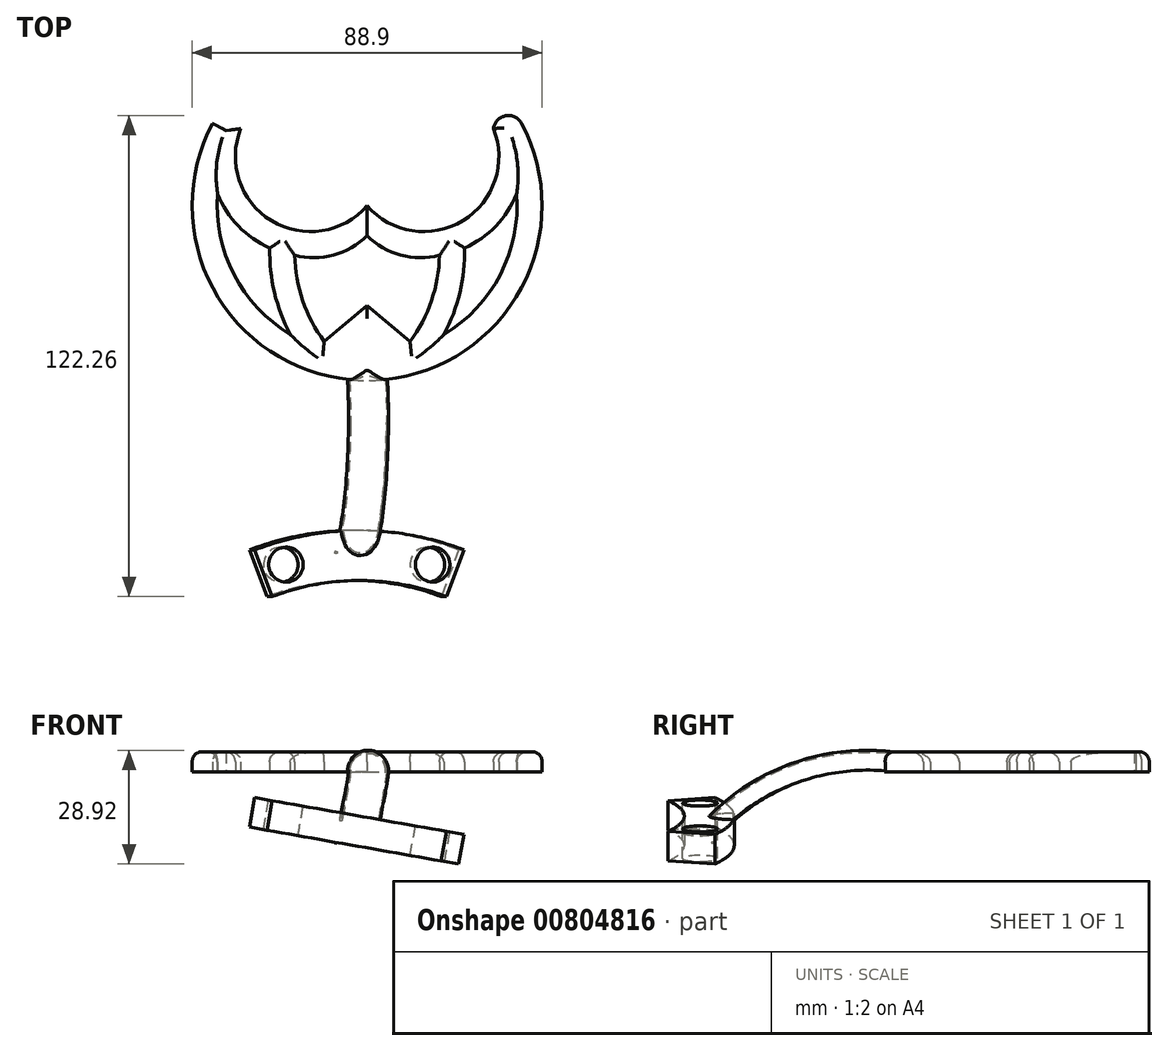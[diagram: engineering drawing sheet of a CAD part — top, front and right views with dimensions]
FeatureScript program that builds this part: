
annotation { "Feature Type Name" : "Feature", "Feature Type Description" : "" }
export const myFeature = defineFeature(function(context is Context, id is Id, definition is map)
    precondition{}
    {
        {
            var Q0;
            Q0=qCreatedBy(makeId("Top.planeOp"),FACE);
            var sketch = newSketch(context, id + "F0", { "sketchPlane" : qUnion([Q0])});
            skArc(sketch, "E0", {"start": v(-39.25, 20.86) * mm, "mid": v(0, -44.45) * mm, "end": v(39.25, 20.86) * mm});
            skPoint(sketch, "E1", {"position": v(0, -44.45) * mm});
            skArc(sketch, "E2", {"start": v(-39.25, 20.86) * mm, "mid": v(-35.2, 22.82) * mm, "end": v(-32.1, 19.54) * mm});
            skLineSegment(sketch, "E3", {"start": v(-35.88, 19.08) * mm, "end": v(-39.25, 20.86) * mm});
            skLineSegment(sketch, "E4", {"start": v(-35.88, 19.08) * mm, "end": v(-32.1, 19.54) * mm});
            skArc(sketch, "E5", {"start": v(-32.1, 19.54) * mm, "mid": v(-24.33, -3.83) * mm, "end": v(0, 0) * mm});
            skPoint(sketch, "E6", {"position": v(0, -25.4) * mm});
            skLineSegment(sketch, "E7", {"start": v(0, -44.45) * mm, "end": v(0, -25.4) * mm});
            skLineSegment(sketch, "E8", {"start": v(0, -25.4) * mm, "end": v(-18.1, -40.6) * mm});
            skArc(sketch, "E9", {"start": v(-17.99, -6.27) * mm, "mid": v(-14.76, -28.08) * mm, "end": v(0, -44.45) * mm});
            skLineSegment(sketch, "E10", {"start": v(0, 0) * mm, "end": v(0, -7.62) * mm});
            skArc(sketch, "E11", {"start": v(-18.39, -12.6) * mm, "mid": v(-8.53, -12.58) * mm, "end": v(0, -7.62) * mm});
            skArc(sketch, "E12", {"start": v(-24.73, -10.77) * mm, "mid": v(-23.55, -22.07) * mm, "end": v(-19.55, -32.7) * mm});
            skArc(sketch, "E13", {"start": v(-37.99, 2.95) * mm, "mid": v(-32.7, -5.2) * mm, "end": v(-24.73, -10.77) * mm});
            skArc(sketch, "E14", {"start": v(-37.99, 2.95) * mm, "mid": v(-33.84, -17.5) * mm, "end": v(-19.55, -32.7) * mm});
            skArc(sketch, "E15.MirrorCS", {"start": v(32.1, 19.54) * mm, "mid": v(24.33, -3.83) * mm, "end": v(0, 0) * mm});
            skArc(sketch, "E16.MirrorCS", {"start": v(39.25, 20.86) * mm, "mid": v(35.2, 22.82) * mm, "end": v(32.1, 19.54) * mm});
            skArc(sketch, "E17.MirrorCS", {"start": v(39.25, 20.86) * mm, "mid": v(0, -44.45) * mm, "end": v(-39.25, 20.86) * mm});
            skArc(sketch, "E18.MirrorCS", {"start": v(37.99, 2.95) * mm, "mid": v(33.84, -17.5) * mm, "end": v(19.55, -32.7) * mm});
            skArc(sketch, "E19.MirrorCS", {"start": v(24.73, -10.77) * mm, "mid": v(23.55, -22.07) * mm, "end": v(19.55, -32.7) * mm});
            skArc(sketch, "E20.MirrorCS", {"start": v(17.99, -6.27) * mm, "mid": v(14.76, -28.08) * mm, "end": v(0, -44.45) * mm});
            skLineSegment(sketch, "E21.MirrorCS", {"start": v(0, -25.4) * mm, "end": v(18.1, -40.6) * mm});
            skArc(sketch, "E22.MirrorCS", {"start": v(37.99, 2.95) * mm, "mid": v(32.7, -5.2) * mm, "end": v(24.73, -10.77) * mm});
            skArc(sketch, "E23.MirrorCS", {"start": v(18.39, -12.6) * mm, "mid": v(8.53, -12.58) * mm, "end": v(0, -7.62) * mm});
            skSolve(sketch);
        }
        {
            var Q0;
            Q0=makeQuery(id+"F0.imprint","IMPRINT",FACE,{"disambiguationData":[TD([[makeQuery(id+"F0.imprint","IMPRINT",EDGE,{"derivedFrom":sQuery(id+"F0.wireOp",EDGE,"E2")}),-1.0]])]});
            var Q1;
            {var subQ9=sQuery(id+"F0.wireOp",EDGE,"E3");Q1=makeQuery(id+"F0.imprint","IMPRINT",FACE,{"disambiguationData":[TD([[makeQuery(id+"F0.imprint","IMPRINT",EDGE,{"derivedFrom":subQ9}),1.0]])]});}
            var Q2;
            {var subQ0=sQuery(id+"F0.wireOp",EDGE,"E10");Q2=makeQuery(id+"F0.imprint","IMPRINT",FACE,{"disambiguationData":[TD([[makeQuery(id+"F0.imprint","IMPRINT",EDGE,{"derivedFrom":subQ0}),-1.0]])]});}
            var Q3;
            {var subQ0=sQuery(id+"F0.wireOp",EDGE,"E10");Q3=makeQuery(id+"F0.imprint","IMPRINT",FACE,{"disambiguationData":[TD([[makeQuery(id+"F0.imprint","IMPRINT",EDGE,{"derivedFrom":subQ0}),1.0]])]});}
            var Q4;
            {var subQ0=sQuery(id+"F0.wireOp",EDGE,"E7");Q4=makeQuery(id+"F0.imprint","IMPRINT",FACE,{"disambiguationData":[TD([[makeQuery(id+"F0.imprint","IMPRINT",EDGE,{"derivedFrom":subQ0}),1.0]])]});}
            var Q5;
            {var subQ0=sQuery(id+"F0.wireOp",EDGE,"E17.MirrorCS");var subQ1=sQuery(id+"F0.wireOp",EDGE,"E8");var subQ2=makeQuery(id+"F0.imprint","INTERSECT",VERTEX,{"derivedFrom":[subQ1,subQ0]});Q5=makeQuery(id+"F0.imprint","IMPRINT",FACE,{"disambiguationData":[TD([[makeQuery(id+"F0.imprint","IMPRINT",EDGE,{"disambiguationData":[TD([[subQ2,1.0]])],"derivedFrom":subQ1}),1.0]])]});}
            var Q6;
            {var subQ0=sQuery(id+"F0.wireOp",EDGE,"E7");Q6=makeQuery(id+"F0.imprint","IMPRINT",FACE,{"disambiguationData":[TD([[makeQuery(id+"F0.imprint","IMPRINT",EDGE,{"derivedFrom":subQ0}),-1.0]])]});}
            var Q7;
            {var subQ1=sQuery(id+"F0.wireOp",EDGE,"E17.MirrorCS");var subQ3=sQuery(id+"F0.wireOp",EDGE,"E21.MirrorCS");var subQ4=makeQuery(id+"F0.imprint","INTERSECT",VERTEX,{"derivedFrom":[subQ1,subQ3]});Q7=makeQuery(id+"F0.imprint","IMPRINT",FACE,{"disambiguationData":[TD([[makeQuery(id+"F0.imprint","IMPRINT",EDGE,{"disambiguationData":[TD([[subQ4,1.0]])],"derivedFrom":subQ3}),-1.0]])]});}
            var Q8;
            {var subQ1=sQuery(id+"F0.wireOp",EDGE,"E16.MirrorCS");Q8=makeQuery(id+"F0.imprint","IMPRINT",FACE,{"disambiguationData":[TD([[makeQuery(id+"F0.imprint","IMPRINT",EDGE,{"derivedFrom":subQ1}),1.0]])]});}
            extrude(context, id + "F1", {"entities" : qUnion([Q0, Q1, Q2, Q3, Q4, Q5, Q6, Q7, Q8]), "depth" : 5.08 * mm});
        }
        {
            var Q0;
            Q0=makeQuery(id+"F1.opExtrude","CAP_EDGE",EDGE,{"disambiguationData":[OSD([sQuery(id+"F0.wireOp",EDGE,"E5")])],"isStart":false});
            var Q1;
            Q1=makeQuery(id+"F1.opExtrude","CAP_EDGE",EDGE,{"disambiguationData":[OSD([sQuery(id+"F0.wireOp",EDGE,"E15.MirrorCS")])],"isStart":false});
            var Q2;
            Q2=makeQuery(id+"F1.opExtrude","CAP_EDGE",EDGE,{"disambiguationData":[OSD([sQuery(id+"F0.wireOp",EDGE,"E2")])],"isStart":false});
            var Q3;
            Q3=makeQuery(id+"F1.opExtrude","CAP_EDGE",EDGE,{"disambiguationData":[OSD([sQuery(id+"F0.wireOp",EDGE,"E17.MirrorCS")])],"isStart":false});
            var Q4;
            Q4=makeQuery(id+"F1.opExtrude","CAP_EDGE",EDGE,{"disambiguationData":[OSD([sQuery(id+"F0.wireOp",EDGE,"E16.MirrorCS")])],"isStart":false});
            var Q5;
            Q5=makeQuery(id+"F1.opExtrude","CAP_EDGE",EDGE,{"disambiguationData":[OSD([sQuery(id+"F0.wireOp",EDGE,"E13")])],"isStart":false});
            var Q6;
            Q6=makeQuery(id+"F1.opExtrude","CAP_EDGE",EDGE,{"disambiguationData":[OSD([sQuery(id+"F0.wireOp",EDGE,"E14")])],"isStart":false});
            var Q7;
            Q7=makeQuery(id+"F1.opExtrude","CAP_EDGE",EDGE,{"disambiguationData":[OSD([sQuery(id+"F0.wireOp",EDGE,"E12")])],"isStart":false});
            var Q8;
            Q8=makeQuery(id+"F1.opExtrude","CAP_EDGE",EDGE,{"disambiguationData":[OSD([sQuery(id+"F0.wireOp",EDGE,"E11")])],"isStart":false});
            var Q9;
            Q9=makeQuery(id+"F1.opExtrude","CAP_EDGE",EDGE,{"disambiguationData":[OSD([sQuery(id+"F0.wireOp",EDGE,"E9")])],"isStart":false});
            var Q10;
            Q10=makeQuery(id+"F1.opExtrude","CAP_EDGE",EDGE,{"disambiguationData":[OSD([sQuery(id+"F0.wireOp",EDGE,"E8")])],"isStart":false});
            var Q11;
            Q11=makeQuery(id+"F1.opExtrude","CAP_EDGE",EDGE,{"disambiguationData":[OSD([sQuery(id+"F0.wireOp",EDGE,"E21.MirrorCS")])],"isStart":false});
            var Q12;
            Q12=makeQuery(id+"F1.opExtrude","CAP_EDGE",EDGE,{"disambiguationData":[OSD([sQuery(id+"F0.wireOp",EDGE,"E23.MirrorCS")])],"isStart":false});
            var Q13;
            Q13=makeQuery(id+"F1.opExtrude","CAP_EDGE",EDGE,{"disambiguationData":[OSD([sQuery(id+"F0.wireOp",EDGE,"E20.MirrorCS")])],"isStart":false});
            var Q14;
            Q14=makeQuery(id+"F1.opExtrude","CAP_EDGE",EDGE,{"disambiguationData":[OSD([sQuery(id+"F0.wireOp",EDGE,"E19.MirrorCS")])],"isStart":false});
            var Q15;
            Q15=makeQuery(id+"F1.opExtrude","CAP_EDGE",EDGE,{"disambiguationData":[OSD([sQuery(id+"F0.wireOp",EDGE,"E22.MirrorCS")])],"isStart":false});
            var Q16;
            Q16=makeQuery(id+"F1.opExtrude","CAP_EDGE",EDGE,{"disambiguationData":[OSD([sQuery(id+"F0.wireOp",EDGE,"E18.MirrorCS")])],"isStart":false});
            fillet(context, id + "F2", {"entities" : qUnion([Q0, Q1, Q2, Q3, Q4, Q5, Q6, Q7, Q8, Q9, Q10, Q11, Q12, Q13, Q14, Q15, Q16]), "radius" : 2.54 * mm, "tangentPropagation" : true, "allowEdgeOverflow" : false});
        }
        {
            var Q0;
            Q0=qCreatedBy(makeId("Front.planeOp"),FACE);
            cPlane(context, id + "F3", {"entities" : qUnion([Q0]), "cplaneType" : CPlaneType.OFFSET, "offset" : 41.9 * mm, "width" : 152.4 * mm, "height" : 152.4 * mm});
        }
        {
            var Q0;
            Q0=qCreatedBy(id+"F3.planeOp",FACE);
            var sketch = newSketch(context, id + "F4", { "sketchPlane" : qUnion([Q0])});
            skArc(sketch, "E24", {"start": v(5.08, 0) * mm, "mid": v(0, 5.08) * mm, "end": v(-5.08, 0) * mm});
            skArc(sketch, "E25.0", {"start": v(4.57, 0) * mm, "mid": v(0, 4.57) * mm, "end": v(-4.57, 0) * mm});
            skLineSegment(sketch, "E26", {"start": v(-5.08, 0) * mm, "end": v(-4.57, 0) * mm});
            skLineSegment(sketch, "E27", {"start": v(4.57, 0) * mm, "end": v(5.08, 0) * mm});
            skSolve(sketch);
        }
        {
            var Q0;
            Q0=sQuery(id+"F0.wireOp",EDGE,"E7");
            cPlane(context, id + "F5", {"entities" : qUnion([Q0]), "cplaneType" : CPlaneType.LINE_ANGLE, "offset" : 25.4 * mm, "angle" : 10 * degree, "width" : 152.4 * mm, "height" : 152.4 * mm});
        }
        {
            var Q0;
            Q0=qCreatedBy(id+"F5.planeOp",FACE);
            cPlane(context, id + "F6", {"entities" : qUnion([Q0]), "cplaneType" : CPlaneType.OFFSET, "offset" : 19.05 * mm, "oppositeDirection" : true, "width" : 152.4 * mm, "height" : 152.4 * mm});
        }
        {
            var Q0;
            Q0=qCreatedBy(id+"F6.planeOp",FACE);
            var sketch = newSketch(context, id + "F7", { "sketchPlane" : qUnion([Q0])});
            skArc(sketch, "E28", {"start": v(26.99, -87.49) * mm, "mid": v(0, -82.55) * mm, "end": v(-26.99, -87.49) * mm});
            skArc(sketch, "E29.0", {"start": v(22.49, -99.37) * mm, "mid": v(0, -95.25) * mm, "end": v(-22.49, -99.37) * mm});
            skPoint(sketch, "E30", {"position": v(0, -82.55) * mm});
            skLineSegment(sketch, "E31", {"start": v(-26.99, -87.49) * mm, "end": v(-22.49, -99.37) * mm});
            skLineSegment(sketch, "E32", {"start": v(26.99, -87.49) * mm, "end": v(22.49, -99.37) * mm});
            skSolve(sketch);
        }
        {
            var Q0;
            Q0=sQuery(id+"F7.wireOp",EDGE,"E28");
            cPoint(context, id + "F8", {"entities" : qUnion([Q0]), "parameter" : 0.5});
        }
        {
            var Q0;
            Q0=makeQuery(id+"F2.opFillet","BLEND_EDGE",EDGE,{"blendedFrom":[makeQuery(id+"F1.opExtrude","CAP_EDGE",EDGE,{"disambiguationData":[OSD([sQuery(id+"F0.wireOp",EDGE,"E5")])],"isStart":false}),makeQuery(id+"F1.opExtrude","CAP_EDGE",EDGE,{"disambiguationData":[OSD([sQuery(id+"F0.wireOp",EDGE,"E15.MirrorCS")])],"isStart":false})],"blendedInto":[]});
            cPoint(context, id + "F9", {"entities" : qUnion([Q0]), "parameter" : 0.5});
        }
        {
            var Q0;
            Q0=qCreatedBy(id+"F8",VERTEX);
            var Q1;
            Q1=sQuery(id+"F4.wireOp",VERTEX,"E25.0.center");
            var Q2;
            Q2=qCreatedBy(id+"F9",VERTEX);
            cPlane(context, id + "F10", {"entities" : qUnion([Q0, Q1, Q2]), "cplaneType" : CPlaneType.THREE_POINT, "offset" : 25.4 * mm, "width" : 152.4 * mm, "height" : 152.4 * mm});
        }
        {
            var Q0;
            Q0=qCreatedBy(id+"F10.planeOp",FACE);
            var sketch = newSketch(context, id + "F11", { "sketchPlane" : qUnion([Q0])});
            skArc(sketch, "E33", {"start": v(-41.9, 0) * mm, "mid": v(-67.94, -3.23) * mm, "end": v(-88.9, -19.02) * mm});
            skSolve(sketch);
        }
        {
            var Q0;
            Q0=makeQuery(id+"F4.imprint","IMPRINT",FACE,{"disambiguationData":[TD([[makeQuery(id+"F4.imprint","IMPRINT",EDGE,{"derivedFrom":sQuery(id+"F4.wireOp",EDGE,"E24")}),1.0]])]});
            var Q1;
            Q1=sQuery(id+"F11.wireOp",EDGE,"E33");
            sweep(context, id + "F12", {"operationType" : NewBodyOperationType.ADD, "profiles" : qUnion([Q0]), "path" : qUnion([Q1])});
        }
        {
            var Q0;
            Q0=makeQuery(id+"F7.imprint","IMPRINT",FACE,{"disambiguationData":[TD([[makeQuery(id+"F7.imprint","IMPRINT",EDGE,{"derivedFrom":sQuery(id+"F7.wireOp",EDGE,"E28")}),1.0]])]});
            extrude(context, id + "F13", {"entities" : qUnion([Q0]), "operationType" : NewBodyOperationType.ADD, "depth" : 7.62 * mm});
        }
        {
            var Q0;
            {var subQ0=sQuery(id+"F7.wireOp",EDGE,"E29.0");var subQ2=sQuery(id+"F7.wireOp",EDGE,"E28");var subQ3=sQuery(id+"F7.wireOp",EDGE,"E32");var subQ4=sQuery(id+"F7.wireOp",EDGE,"E31");Q0=makeQuery(id+"F13.boolean.opBoolean","SPLIT",FACE,{"disambiguationData":[TD([makeQuery(id+"F13.opExtrude","SWEPT_FACE",FACE,{"disambiguationData":[OSD([subQ0])]})])],"derivedFrom":makeQuery(id+"F13.opExtrude","CAP_FACE",FACE,{"disambiguationData":[OSD([subQ2,subQ0,subQ4,subQ3])],"isStart":false})});}
            var sketch = newSketch(context, id + "F14", { "sketchPlane" : qUnion([Q0])});
            skCircle(sketch, "E34", {"center": v(-18.92, -91.22) * mm, "radius": 4.45 * mm});
            skCircle(sketch, "E35", {"center": v(18.92, -91.22) * mm, "radius": 4.45 * mm});
            skSolve(sketch);
        }
        {
            var Q0;
            Q0=qSketchRegion(id+"F14",true);
            extrude(context, id + "F15", {"entities" : qUnion([Q0]), "operationType" : NewBodyOperationType.REMOVE, "oppositeDirection" : true, "depth" : 25.4 * mm});
        }
    });
